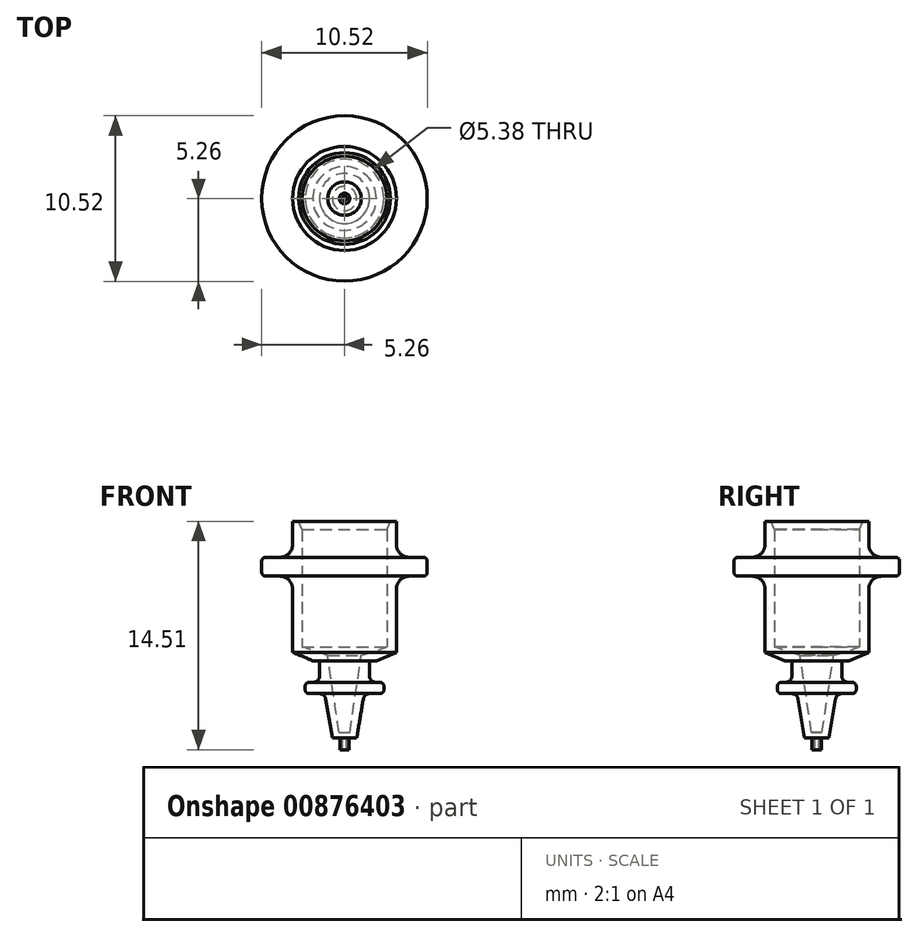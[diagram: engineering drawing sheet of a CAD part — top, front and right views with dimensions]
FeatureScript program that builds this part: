
annotation { "Feature Type Name" : "Feature", "Feature Type Description" : "" }
export const myFeature = defineFeature(function(context is Context, id is Id, definition is map)
    precondition{}
    {
        {
            var Q0;
            Q0=qCreatedBy(makeId("Front.planeOp"),FACE);
            var sketch = newSketch(context, id + "F0", { "sketchPlane" : qUnion([Q0])});
            skLineSegment(sketch, "E0", {"start": v(0.12, 0) * mm, "end": v(0.3, 0) * mm});
            skLineSegment(sketch, "E1", {"start": v(0.3, 0) * mm, "end": v(0.3, 0.76) * mm});
            skLineSegment(sketch, "E2", {"start": v(0.3, 0.76) * mm, "end": v(0.78, 0.76) * mm});
            skLineSegment(sketch, "E3", {"start": v(0.77, 0.76) * mm, "end": v(1.25, 3.57) * mm});
            skLineSegment(sketch, "E4", {"start": v(1.25, 3.57) * mm, "end": v(2.5, 3.57) * mm});
            skLineSegment(sketch, "E5", {"start": v(2.5, 3.57) * mm, "end": v(2.5, 4.3) * mm});
            skLineSegment(sketch, "E6", {"start": v(2.5, 4.3) * mm, "end": v(1.58, 4.3) * mm});
            skLineSegment(sketch, "E7", {"start": v(1.58, 4.3) * mm, "end": v(1.58, 5.66) * mm});
            skLineSegment(sketch, "E8", {"start": v(1.58, 5.66) * mm, "end": v(2.02, 5.66) * mm});
            skLineSegment(sketch, "E9", {"start": v(3.3, 6.2) * mm, "end": v(2.02, 5.66) * mm});
            skLineSegment(sketch, "E10", {"start": v(3.3, 6.2) * mm, "end": v(3.3, 11.03) * mm});
            skLineSegment(sketch, "E11", {"start": v(3.3, 11.03) * mm, "end": v(5.25, 11.03) * mm});
            skLineSegment(sketch, "E12", {"start": v(5.25, 11.03) * mm, "end": v(5.25, 12.23) * mm});
            skLineSegment(sketch, "E13", {"start": v(5.25, 12.23) * mm, "end": v(3.3, 12.23) * mm});
            skLineSegment(sketch, "E14", {"start": v(3.3, 12.23) * mm, "end": v(3.3, 14.5) * mm});
            skLineSegment(sketch, "E15", {"start": v(3.3, 14.5) * mm, "end": v(2.91, 14.5) * mm});
            skLineSegment(sketch, "E16", {"start": v(2.91, 14.51) * mm, "end": v(2.7, 13.98) * mm});
            skLineSegment(sketch, "E17", {"start": v(2.69, 13.98) * mm, "end": v(2.7, 6.54) * mm});
            skLineSegment(sketch, "E18", {"start": v(2.7, 6.54) * mm, "end": v(1.06, 5.99) * mm});
            skLineSegment(sketch, "E19", {"start": v(1.06, 5.99) * mm, "end": v(0.34, 1.1) * mm});
            skLineSegment(sketch, "E20", {"start": v(0.34, 1.1) * mm, "end": v(0.13, 1.1) * mm});
            skLineSegment(sketch, "E21", {"start": v(0.13, 1.1) * mm, "end": v(0.13, 0) * mm});
            skLineSegment(sketch, "E22", {"start": v(0, 0) * mm, "end": v(0, 1.24) * mm, "construction": true});
            skSolve(sketch);
        }
        {
            var Q0;
            Q0=makeQuery(id+"F0.imprint","IMPRINT",FACE,{"disambiguationData":[TD([[makeQuery(id+"F0.imprint","IMPRINT",EDGE,{"derivedFrom":sQuery(id+"F0.wireOp",EDGE,"E0")}),1.0]])]});
            var Q1;
            Q1=sQuery(id+"F0.wireOp",EDGE,"E22");
            revolve(context, id + "F1", {"surfaceOperationType" : NewSurfaceOperationType.NEW, "entities" : qUnion([Q0]), "axis" : qUnion([Q1]), "revolveType" : RevolveType.FULL});
        }
        {
            var Q0;
            Q0=makeQuery(id+"F1.opRevolve","SWEPT_EDGE",EDGE,{"disambiguationData":[OSD([sQuery(id+"F0.wireOp",EDGE,"E12"),sQuery(id+"F0.wireOp",EDGE,"E13")])]});
            var Q1;
            Q1=makeQuery(id+"F1.opRevolve","SWEPT_EDGE",EDGE,{"disambiguationData":[OSD([sQuery(id+"F0.wireOp",EDGE,"E11"),sQuery(id+"F0.wireOp",EDGE,"E12")])]});
            var Q2;
            Q2=makeQuery(id+"F1.opRevolve","SWEPT_EDGE",EDGE,{"disambiguationData":[OSD([sQuery(id+"F0.wireOp",EDGE,"E5"),sQuery(id+"F0.wireOp",EDGE,"E6")])]});
            var Q3;
            Q3=makeQuery(id+"F1.opRevolve","SWEPT_EDGE",EDGE,{"disambiguationData":[OSD([sQuery(id+"F0.wireOp",EDGE,"E4"),sQuery(id+"F0.wireOp",EDGE,"E5")])]});
            fillet(context, id + "F2", {"entities" : qUnion([Q0, Q1, Q2, Q3]), "radius" : 0.25 * mm, "tangentPropagation" : true, "allowEdgeOverflow" : false});
        }
        {
            var Q0;
            Q0=makeQuery(id+"F1.opRevolve","SWEPT_EDGE",EDGE,{"disambiguationData":[OSD([sQuery(id+"F0.wireOp",EDGE,"E13"),sQuery(id+"F0.wireOp",EDGE,"E14")])]});
            var Q1;
            Q1=makeQuery(id+"F1.opRevolve","SWEPT_EDGE",EDGE,{"disambiguationData":[OSD([sQuery(id+"F0.wireOp",EDGE,"E10"),sQuery(id+"F0.wireOp",EDGE,"E11")])]});
            fillet(context, id + "F3", {"entities" : qUnion([Q0, Q1]), "radius" : 0.8 * mm, "tangentPropagation" : true, "allowEdgeOverflow" : false});
        }
        {
            var Q0;
            Q0=makeQuery(id+"F1.opRevolve","SWEPT_EDGE",EDGE,{"disambiguationData":[OSD([sQuery(id+"F0.wireOp",EDGE,"E6"),sQuery(id+"F0.wireOp",EDGE,"E7")])]});
            var Q1;
            Q1=makeQuery(id+"F1.opRevolve","SWEPT_EDGE",EDGE,{"disambiguationData":[OSD([sQuery(id+"F0.wireOp",EDGE,"E3"),sQuery(id+"F0.wireOp",EDGE,"E4")])]});
            fillet(context, id + "F4", {"entities" : qUnion([Q0, Q1]), "radius" : 0.4 * mm, "tangentPropagation" : true, "allowEdgeOverflow" : false});
        }
    });
